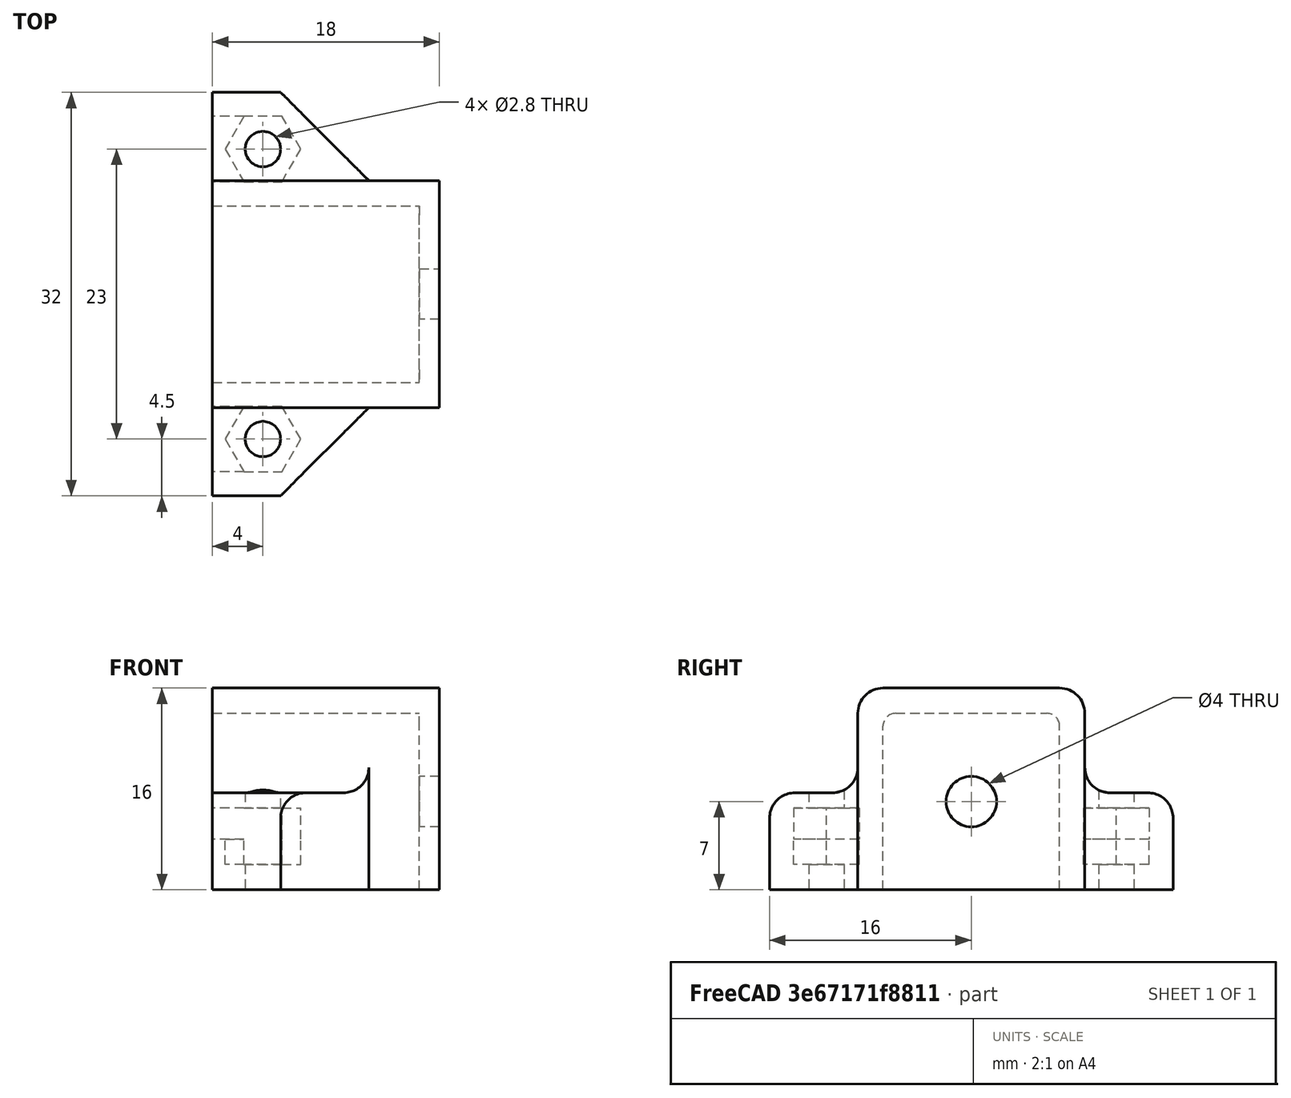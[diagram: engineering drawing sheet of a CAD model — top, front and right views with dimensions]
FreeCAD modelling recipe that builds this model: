
FCSTD DOCUMENT  (FreeCAD 0.19R24276 (Git))
Label: PB3D_TriPlate_MotWireRet
License: All rights reserved
LicenseURL: http://en.wikipedia.org/wiki/All_rights_reserved
objects: Sketcher::SketchObject×8, PartDesign::Pocket×6, PartDesign::Plane×2, Spreadsheet::Sheet×1, PartDesign::Pad×1, PartDesign::Body×1, App::Part×1, Mesh::Feature×1
note: 25 computed .brp shape members not serialized (recipe doc carries the construction recipe); baked Part::Feature solids carry a one-line shape summary decoded from their .brp

FEATURE [Spreadsheet::Sheet] Spreadsheet  label="params"
  cells = A2=M2 Bolt Clearances; C2=M2.5 Bolt Clearances; E2=M3 Bolt Clearances; A3=Hole Clear Diam; B3(m2_hole_clear_diam)==2.5mm; C3=Hole Clear Diam; D3(m25_hole_clear_diam)==2.8mm; E3=Hole Clear Diam; F3(m3_hole_clear_diam)==3.3mm; A4=Head Clear Diam; B4(m2_head_clear_diam)==4mm; C4=Head Clear Diam; D4(m25_head_clear_diam)==5mm; E4=Head Clear Diam; F4(m3_head_clear_diam)==6.1mm; A5=Head Min Depth; B5(m2_head_min_depth)==1.3mm; C5=Head Min Depth; D5(m25_head_min_depth)==1.6mm; E5=Head Min Depth; F5(m3_head_min_depth)==1.8mm; A6=Nut Clear Flat; B6(m2_nut_clear_flat)==4.2mm; C6=Nut Clear Flat; D6(m25_nut_clear_flat)==5.2mm; E6=Nut Clear Flat; F6(m3_nut_clear_flat)==5.8mm; A7=Nut Min Depth; B7(m2_nut_min_depth)==1.75mm; C7=Nut Min Depth; D7(m25_nut_min_depth)==2mm; E7=Nut Min Depth; F7(m3_nut_min_depth)==2.4mm; A9=Mot Wire Ret Dims; A10=Std Rad; B10(std_rad)==2mm; C10=Foot Width; D10(foot_width)==7mm; E10=Hole Loc L; F10(hole_loc_l)==4mm; A11=Arch Height; B11(arch_height)==14mm; C11=Foot Height; D11(foot_height)==hsunk_z + hsunk_height + hslot_height + 1.2mm; E11=Hole Loc W; F11(hole_loc_w)==arch_width + foot_tot_width; A12=Arch Width; B12(arch_width)==14mm; E12=Hex Sunk Z; F12(hsunk_z)==2mm; A13=Arch Leng; B13(arch_leng)==18mm; C13=Foot Tot Width; D13(foot_tot_width)==foot_width + arch_wallthick; E13=Hex Sunk Height; F13(hsunk_height)==m25_nut_min_depth; A14=Arch Wall Thick; B14(arch_wallthick)==2mm; E14=Hex Slot Z; F14(hslot_z)==hsunk_z + hsunk_height; C15=Back Wall Thick; D15(back_wall_thick)==1.6mm; E15=Hex Slot Height; F15(hslot_height)==m25_nut_min_depth + 0.5mm; A16=Tot Width; B16(tot_width)==arch_width + 2 * foot_width + 2 * arch_wallthick
FEATURE [Sketcher::SketchObject] Sketch
  FullyConstrained = true
  MapMode = 5
  Placement = pos=(0,0,0) rot=(0.57735,0.57735,0.57735;2.0944rad)
  Support = -> [YZ_Plane001]
  expr: Constraints[42] = <<params>>.std_rad
  expr: Constraints[46] = <<params>>.arch_wallthick
  expr: Constraints[43] = <<params>>.arch_width
  expr: Constraints[50] = <<params>>.foot_width
  expr: Constraints[44] = <<params>>.arch_height
  expr: Constraints[48] = <<params>>.std_rad / 2
  expr: Constraints[45] = <<params>>.arch_wallthick
  expr: Constraints[51] = <<params>>.foot_height
  sketch-geometry (22):
    g0: LineSegment StartX=-16 StartY=0 StartZ=0 EndX=-7 EndY=0 EndZ=0
    g1: LineSegment StartX=7 StartY=0 StartZ=0 EndX=16 EndY=0 EndZ=0
    g2: LineSegment StartX=-7 StartY=0 StartZ=0 EndX=-7 EndY=13 EndZ=0
    g3: LineSegment StartX=-6 StartY=14 StartZ=0 EndX=6 EndY=14 EndZ=0
    g4: LineSegment StartX=7 StartY=0 StartZ=0 EndX=7 EndY=13 EndZ=0
    g5: LineSegment StartX=-16 StartY=0 StartZ=0 EndX=-16 EndY=5.7 EndZ=0
    g6: LineSegment StartX=-14 StartY=7.7 StartZ=0 EndX=-11 EndY=7.7 EndZ=0
    g7: LineSegment StartX=-9 StartY=9.7 StartZ=0 EndX=-9 EndY=14 EndZ=0
    g8: LineSegment StartX=-7 StartY=16 StartZ=0 EndX=7 EndY=16 EndZ=0
    g9: LineSegment StartX=9 StartY=14 StartZ=0 EndX=9 EndY=9.7 EndZ=0
    g10: LineSegment StartX=11 StartY=7.7 StartZ=0 EndX=14 EndY=7.7 EndZ=0
    g11: LineSegment StartX=16 StartY=5.7 StartZ=0 EndX=16 EndY=0 EndZ=0
    g12: LineSegment StartX=0 StartY=0 StartZ=0 EndX=0 EndY=16 EndZ=0
    g13: ArcOfCircle CenterX=-6 CenterY=13 CenterZ=0 NormalX=0 NormalY=0 NormalZ=1 AngleXU=0 Radius=1 StartAngle=1.5708 EndAngle=3.14159
    g14: ArcOfCircle CenterX=6 CenterY=13 CenterZ=0 NormalX=0 NormalY=0 NormalZ=1 AngleXU=0 Radius=1 StartAngle=-9e-16 EndAngle=1.5708
    g15: ArcOfCircle CenterX=7 CenterY=14 CenterZ=0 NormalX=0 NormalY=0 NormalZ=1 AngleXU=0 Radius=2 StartAngle=0 EndAngle=1.5708
    g16: ArcOfCircle CenterX=-7 CenterY=14 CenterZ=0 NormalX=0 NormalY=0 NormalZ=1 AngleXU=0 Radius=2 StartAngle=1.5708 EndAngle=3.14159
    g17: ArcOfCircle CenterX=11 CenterY=9.7 CenterZ=0 NormalX=0 NormalY=0 NormalZ=1 AngleXU=0 Radius=2 StartAngle=3.14159 EndAngle=4.71239
    g18: ArcOfCircle CenterX=14 CenterY=5.7 CenterZ=0 NormalX=0 NormalY=0 NormalZ=1 AngleXU=0 Radius=2 StartAngle=1e-16 EndAngle=1.5708
    g19: ArcOfCircle CenterX=-14 CenterY=5.7 CenterZ=0 NormalX=0 NormalY=0 NormalZ=1 AngleXU=0 Radius=2 StartAngle=1.5708 EndAngle=3.14159
    g20: ArcOfCircle CenterX=-11 CenterY=9.7 CenterZ=0 NormalX=0 NormalY=0 NormalZ=1 AngleXU=0 Radius=2 StartAngle=4.71239 EndAngle=6.28319
    g21: LineSegment StartX=-7 StartY=0 StartZ=0 EndX=7 EndY=0 EndZ=0
  constraints (55):
    c: PointOnObject(g0,g-1)
    c: PointOnObject(g0,g-1)
    c: PointOnObject(g1,g-1)
    c: Equal(g1,g0)
    c: Symmetric(g0,g1,g-1)
    c: Coincident(g2,g0)
    c: Vertical(g2)
    c: Horizontal(g3)
    c: Coincident(g4,g1)
    c: Vertical(g4)
    c: Coincident(g5,g0)
    c: Vertical(g5)
    c: Horizontal(g6)
    c: Vertical(g7)
    c: Horizontal(g8)
    c: Vertical(g9)
    c: Horizontal(g10)
    c: Coincident(g11,g1)
    c: Vertical(g11)
    c: Coincident(g12,g-1)
    c: PointOnObject(g12,g-2)
    c: Tangent(g2,g13) = 1.5708
    c: Tangent(g3,g13) = 1.5708
    c: Tangent(g3,g14) = 1.5708
    c: Tangent(g4,g14) = -1.5708
    c: Tangent(g9,g15) = 1.5708
    c: Tangent(g8,g15) = 1.5708
    c: Tangent(g8,g16) = 1.5708
    c: Tangent(g7,g16) = 1.5708
    c: Tangent(g9,g17) = -1.5708
    c: Tangent(g10,g17) = -1.5708
    c: Tangent(g10,g18) = 1.5708
    c: Tangent(g11,g18) = 1.5708
    c: Tangent(g6,g19) = 1.5708
    c: Tangent(g5,g19) = 1.5708
    c: Tangent(g7,g20) = -1.5708
    c: Tangent(g6,g20) = -1.5708
    c: Symmetric(g8,g8,g12)
    c: Equal(g18,g17)
    c: Equal(g17,g15)
    c: Equal(g16,g20)
    c: Equal(g20,g19)
    c: Radius(g18) = 2
    c: DistanceX(g0,g1) = 14
    c: DistanceY(g-1,g3) = 14
    c: DistanceY(g3,g8) = 2
    c: DistanceX(g4,g9) = 2
    c: Equal(g13,g14)
    c: Radius(g14) = 1
    c: Equal(g16,g15)
    c: DistanceX(g9,g1) = 7
    c: DistanceY(g1,g10) = 7.7
    c: Equal(g11,g5)
    c: Coincident(g21,g1)
    c: Coincident(g21,g0)
FEATURE [PartDesign::Pad] Pad  label="MainExt"
  Direction = (1,1,1)
  Length = 18
  Length2 = 100
  Placement = pos=(0,0,0) rot=(0.57735,0.57735,0.57735;2.0944rad)
  Profile = -> Sketch
  Type = 0
  expr: Length = <<params>>.arch_leng
FEATURE [PartDesign::Plane] DatumPlane  label="Datum_HexSunk"
  AttachmentOffset = pos=(0,0,2) rot=(0,0,1;0rad)
  Length = 60
  MapMode = 5
  Placement = pos=(0,0,2) rot=(0,0,1;0rad)
  ResizeMode = 0
  Support = -> [XY_Plane001]
  Width = 60
  expr: .AttachmentOffset.Base.z = <<params>>.hsunk_z
FEATURE [PartDesign::Plane] DatumPlane001  label="Datum_HexSlot"
  AttachmentOffset = pos=(0,0,4) rot=(0,0,1;0rad)
  Length = 60
  MapMode = 5
  Placement = pos=(0,0,4) rot=(0,0,1;0rad)
  ResizeMode = 0
  Support = -> [XY_Plane001]
  Width = 60
  expr: .AttachmentOffset.Base.z = <<params>>.hslot_z
FEATURE [Sketcher::SketchObject] Sketch001  label="HoleLoc_Temp"
  FullyConstrained = true
  MapMode = 5
  Support = -> [XY_Plane001]
  expr: Constraints[5] = <<params>>.hole_loc_w
  expr: Constraints[4] = <<params>>.hole_loc_l
  sketch-geometry (2):
    g0: LineSegment StartX=0 StartY=0 StartZ=0 EndX=4 EndY=0 EndZ=0
    g1: LineSegment StartX=4 StartY=11.5 StartZ=0 EndX=4 EndY=-11.5 EndZ=0
  constraints (6):
    c: Coincident(g0,g-1)
    c: PointOnObject(g0,g-1)
    c: Vertical(g1)
    c: Symmetric(g1,g1,g0)
    c: DistanceX(g-1,g0) = 4
    c: DistanceY(g1,g1) = 23
FEATURE [Sketcher::SketchObject] Sketch002  label="HoleLoc"
  FullyConstrained = true
  MapMode = 5
  Support = -> [XY_Plane001]
  expr: Constraints[9] = <<params>>.m25_hole_clear_diam
  expr: Constraints[4] = <<params>>.hole_loc_l
  expr: Constraints[5] = <<params>>.hole_loc_w
  sketch-geometry (4):
    g0: LineSegment StartX=0 StartY=0 StartZ=0 EndX=4 EndY=0 EndZ=0
    g1: LineSegment StartX=4 StartY=11.5 StartZ=0 EndX=4 EndY=-11.5 EndZ=0
    g2: Circle CenterX=4 CenterY=11.5 CenterZ=0 NormalX=0 NormalY=0 NormalZ=1 AngleXU=0 Radius=1.4
    g3: Circle CenterX=4 CenterY=-11.5 CenterZ=0 NormalX=0 NormalY=0 NormalZ=1 AngleXU=0 Radius=1.4
  constraints (10):
    c: Coincident(g0,g-1)
    c: PointOnObject(g0,g-1)
    c: Vertical(g1)
    c: Symmetric(g1,g1,g0)
    c: DistanceX(g-1,g0) = 4
    c: DistanceY(g1,g1) = 23
    c: Coincident(g2,g1)
    c: Coincident(g3,g1)
    c: Equal(g2,g3)
    c: Diameter(g2) = 2.8
FEATURE [PartDesign::Pocket] Pocket  label="MtHoles"
  BaseFeature = -> Pad
  Length = 5
  Length2 = 100
  Placement = pos=(0,0,0) rot=(0.57735,0.57735,0.57735;2.0944rad)
  Profile = -> Sketch002
  Reversed = true
  Type = 1
FEATURE [Sketcher::SketchObject] Sketch003  label="HSunk"
  FullyConstrained = true
  MapMode = 5
  Placement = pos=(0,0,2) rot=(0,0,1;0rad)
  Support = -> [DatumPlane]
  expr: Constraints[45] = <<params>>.m25_nut_clear_flat
  expr: Constraints[4] = <<params>>.hole_loc_l
  expr: Constraints[5] = <<params>>.hole_loc_w
  sketch-geometry (16):
    g0: LineSegment StartX=0 StartY=0 StartZ=0 EndX=4 EndY=0 EndZ=0
    g1: LineSegment StartX=4 StartY=11.5 StartZ=0 EndX=4 EndY=-11.5 EndZ=0
    g2: LineSegment StartX=0.997779 StartY=11.5 StartZ=0 EndX=2.49889 EndY=8.9 EndZ=0
    g3: LineSegment StartX=2.49889 StartY=8.9 StartZ=0 EndX=5.50111 EndY=8.9 EndZ=0
    g4: LineSegment StartX=5.50111 StartY=8.9 StartZ=0 EndX=7.00222 EndY=11.5 EndZ=0
    g5: LineSegment StartX=7.00222 StartY=11.5 StartZ=0 EndX=5.50111 EndY=14.1 EndZ=0
    g6: LineSegment StartX=5.50111 StartY=14.1 StartZ=0 EndX=2.49889 EndY=14.1 EndZ=0
    g7: LineSegment StartX=2.49889 StartY=14.1 StartZ=0 EndX=0.997779 EndY=11.5 EndZ=0
    g8: Circle CenterX=4 CenterY=11.5 CenterZ=0 NormalX=0 NormalY=0 NormalZ=1 AngleXU=0 Radius=3.00222
    g9: LineSegment StartX=7.00222 StartY=-11.5 StartZ=0 EndX=5.50111 EndY=-8.9 EndZ=0
    g10: LineSegment StartX=5.50111 StartY=-8.9 StartZ=0 EndX=2.49889 EndY=-8.9 EndZ=0
    g11: LineSegment StartX=2.49889 StartY=-8.9 StartZ=0 EndX=0.997779 EndY=-11.5 EndZ=0
    g12: LineSegment StartX=0.997779 StartY=-11.5 StartZ=0 EndX=2.49889 EndY=-14.1 EndZ=0
    g13: LineSegment StartX=2.49889 StartY=-14.1 StartZ=0 EndX=5.50111 EndY=-14.1 EndZ=0
    g14: LineSegment StartX=5.50111 StartY=-14.1 StartZ=0 EndX=7.00222 EndY=-11.5 EndZ=0
    g15: Circle CenterX=4 CenterY=-11.5 CenterZ=0 NormalX=0 NormalY=0 NormalZ=1 AngleXU=0 Radius=3.00222
  constraints (38):
    c: Coincident(g0,g-1)
    c: PointOnObject(g0,g-1)
    c: Vertical(g1)
    c: Symmetric(g1,g1,g0)
    c: DistanceX(g-1,g0) = 4
    c: DistanceY(g1,g1) = 23
    c: Coincident(g2,g3)
    c: Coincident(g3,g4)
    c: Coincident(g4,g5)
    c: Coincident(g5,g6)
    c: Coincident(g6,g7)
    c: Coincident(g7,g2)
    c: Equal(g2, g3-g7) x5
    c: PointOnObject(g2,g8)
    c: PointOnObject(g3,g8)
    c: PointOnObject(g4,g8)
    c: PointOnObject(g5,g8)
    c: PointOnObject(g6,g8)
    c: PointOnObject(g7,g8)
    c: Coincident(g8,g1)
    c: Coincident(g9,g10)
    c: Coincident(g10,g11)
    c: Coincident(g11,g12)
    c: Coincident(g12,g13)
    c: Coincident(g13,g14)
    c: Coincident(g14,g9)
    c: Equal(g9, g10-g14) x5
    c: PointOnObject(g9,g15)
    c: PointOnObject(g10,g15)
    c: PointOnObject(g11,g15)
    c: PointOnObject(g12,g15)
    c: PointOnObject(g13,g15)
    c: PointOnObject(g14,g15)
    c: Coincident(g15,g1)
    c: Horizontal(g6)
    c: Horizontal(g10)
    c: Equal(g8,g15)
    c: DistanceY(g2,g6) = 5.2
FEATURE [PartDesign::Pocket] Pocket001  label="HexSunk"
  BaseFeature = -> Pocket
  Length = 2
  Length2 = 100
  Placement = pos=(0,0,0) rot=(0.57735,0.57735,0.57735;2.0944rad)
  Profile = -> Sketch003
  Reversed = true
  Type = 0
  expr: Length = <<params>>.hsunk_height
FEATURE [Sketcher::SketchObject] Sketch004  label="Sketch_HSlot"
  FullyConstrained = true
  MapMode = 5
  Placement = pos=(0,0,4) rot=(0,0,1;0rad)
  Support = -> [DatumPlane001]
  expr: Constraints[53] = <<params>>.m25_nut_clear_flat
  expr: Constraints[4] = <<params>>.hole_loc_l
  expr: Constraints[5] = <<params>>.hole_loc_w
  sketch-geometry (19):
    g0: LineSegment StartX=0 StartY=0 StartZ=0 EndX=4 EndY=0 EndZ=0
    g1: LineSegment StartX=4 StartY=11.5 StartZ=0 EndX=4 EndY=-11.5 EndZ=0
    g2: LineSegment StartX=7.00222 StartY=11.5 StartZ=0 EndX=5.50111 EndY=14.1 EndZ=0
    g3: LineSegment StartX=5.50111 StartY=14.1 StartZ=0 EndX=2.49889 EndY=14.1 EndZ=0
    g4: LineSegment StartX=2.49889 StartY=8.9 StartZ=0 EndX=5.50111 EndY=8.9 EndZ=0
    g5: LineSegment StartX=5.50111 StartY=8.9 StartZ=0 EndX=7.00222 EndY=11.5 EndZ=0
    g6: Circle CenterX=4 CenterY=11.5 CenterZ=0 NormalX=0 NormalY=0 NormalZ=1 AngleXU=0 Radius=3.00222
    g7: LineSegment StartX=7.00222 StartY=-11.5 StartZ=0 EndX=5.50111 EndY=-8.9 EndZ=0
    g8: LineSegment StartX=5.50111 StartY=-8.9 StartZ=0 EndX=2.49889 EndY=-8.9 EndZ=0
    g9: LineSegment StartX=2.49889 StartY=-14.1 StartZ=0 EndX=5.50111 EndY=-14.1 EndZ=0
    g10: LineSegment StartX=5.50111 StartY=-14.1 StartZ=0 EndX=7.00222 EndY=-11.5 EndZ=0
    g11: Circle CenterX=4 CenterY=-11.5 CenterZ=0 NormalX=0 NormalY=0 NormalZ=1 AngleXU=0 Radius=3.00222
    g12: LineSegment StartX=2.49889 StartY=14.1 StartZ=0 EndX=-7.50111 EndY=14.1 EndZ=0
    g13: LineSegment StartX=2.49889 StartY=8.9 StartZ=0 EndX=-7.50111 EndY=8.9 EndZ=0
    g14: LineSegment StartX=-7.50111 StartY=8.9 StartZ=0 EndX=-7.50111 EndY=14.1 EndZ=0
    g15: LineSegment StartX=2.49889 StartY=-14.1 StartZ=0 EndX=-7.50111 EndY=-14.1 EndZ=0
    g16: LineSegment StartX=2.49889 StartY=-8.9 StartZ=0 EndX=-7.50111 EndY=-8.9 EndZ=0
    g17: LineSegment StartX=-7.50111 StartY=-14.1 StartZ=0 EndX=-7.50111 EndY=-8.9 EndZ=0
    g18: LineSegment StartX=-7.50111 StartY=-8.9 StartZ=0 EndX=-7.50111 EndY=8.9 EndZ=0
  constraints (54):
    c: Coincident(g0,g-1)
    c: PointOnObject(g0,g-1)
    c: Vertical(g1)
    c: Symmetric(g1,g1,g0)
    c: DistanceX(g-1,g0) = 4
    c: DistanceY(g1,g1) = 23
    c: Coincident(g2,g3)
    c: Coincident(g4,g5)
    c: Coincident(g5,g2)
    c: Equal(g2,g3)
    c: Equal(g2,g4)
    c: Equal(g2,g5)
    c: PointOnObject(g2,g6)
    c: PointOnObject(g3,g6)
    c: PointOnObject(g4,g6)
    c: PointOnObject(g4,g6)
    c: PointOnObject(g5,g6)
    c: Coincident(g6,g1)
    c: Coincident(g7,g8)
    c: Coincident(g9,g10)
    c: Coincident(g10,g7)
    c: Equal(g7,g8)
    c: Equal(g7,g9)
    c: Equal(g7,g10)
    c: PointOnObject(g7,g11)
    c: PointOnObject(g8,g11)
    c: PointOnObject(g9,g11)
    c: PointOnObject(g9,g11)
    c: PointOnObject(g10,g11)
    c: Coincident(g11,g1)
    c: Horizontal(g3)
    c: Horizontal(g8)
    c: Equal(g6,g11)
    c: Horizontal(g9)
    c: Horizontal(g4)
    c: Coincident(g12,g3)
    c: Horizontal(g12)
    c: Coincident(g13,g4)
    c: Horizontal(g13)
    c: Coincident(g14,g13)
    c: Coincident(g14,g12)
    c: Vertical(g14)
    c: Coincident(g15,g9)
    c: Horizontal(g15)
    c: Coincident(g16,g8)
    c: Horizontal(g16)
    c: Coincident(g17,g15)
    c: Coincident(g17,g16)
    c: Vertical(g17)
    c: Coincident(g18,g16)
    c: Coincident(g18,g13)
    c: Vertical(g18)
    c: Distance(g15) = 10
    c: DistanceY(g9,g7) = 5.2
FEATURE [PartDesign::Pocket] Pocket002  label="HexSlot"
  BaseFeature = -> Pocket001
  Length = 2.5
  Length2 = 100
  Placement = pos=(0,0,0) rot=(0.57735,0.57735,0.57735;2.0944rad)
  Profile = -> Sketch004
  Reversed = true
  Type = 0
  expr: Length = <<params>>.hslot_height
FEATURE [Sketcher::SketchObject] Sketch005
  FullyConstrained = true
  MapMode = 5
  Support = -> [XY_Plane001]
  expr: Constraints[31] = <<params>>.hole_loc_l + <<params>>.m25_hole_clear_diam / 2
  expr: Constraints[30] = <<params>>.arch_leng
  expr: Constraints[29] = <<params>>.foot_width
  expr: Constraints[27] = <<params>>.arch_width + <<params>>.arch_wallthick * 2
  sketch-geometry (12):
    g0: LineSegment StartX=12.4 StartY=9 StartZ=0 EndX=5.4 EndY=16 EndZ=0
    g1: LineSegment StartX=5.4 StartY=16 StartZ=0 EndX=23.4 EndY=16 EndZ=0
    g2: LineSegment StartX=12.4 StartY=9 StartZ=0 EndX=23.4 EndY=9 EndZ=0
    g3: LineSegment StartX=23.4 StartY=16 StartZ=0 EndX=23.4 EndY=9 EndZ=0
    g4: LineSegment StartX=0 StartY=0 StartZ=0 EndX=12.4 EndY=0 EndZ=0
    g5: LineSegment StartX=12.4 StartY=9 StartZ=0 EndX=12.4 EndY=-9 EndZ=0
    g6: LineSegment StartX=12.4 StartY=-9 StartZ=0 EndX=23.4 EndY=-9 EndZ=0
    g7: LineSegment StartX=23.4 StartY=-9 StartZ=0 EndX=23.4 EndY=-16 EndZ=0
    g8: LineSegment StartX=12.4 StartY=-9 StartZ=0 EndX=5.4 EndY=-16 EndZ=0
    g9: LineSegment StartX=5.4 StartY=-16 StartZ=0 EndX=23.4 EndY=-16 EndZ=0
    g10: LineSegment StartX=23.4 StartY=9 StartZ=0 EndX=23.4 EndY=-9 EndZ=0
    g11: LineSegment StartX=5.4 StartY=16 StartZ=0 EndX=5.4 EndY=-16 EndZ=0
  constraints (32):
    c: Coincident(g1,g0)
    c: Horizontal(g1)
    c: Coincident(g2,g0)
    c: Horizontal(g2)
    c: Coincident(g3,g1)
    c: Coincident(g3,g2)
    c: Vertical(g3)
    c: Coincident(g4,g-1)
    c: PointOnObject(g4,g-1)
    c: Coincident(g5,g0)
    c: Vertical(g5)
    c: Symmetric(g0,g5,g4)
    c: Coincident(g6,g5)
    c: Horizontal(g6)
    c: Coincident(g7,g6)
    c: Vertical(g7)
    c: Coincident(g8,g6)
    c: Coincident(g9,g8)
    c: Coincident(g9,g7)
    c: Horizontal(g9)
    c: Coincident(g10,g2)
    c: Coincident(g10,g6)
    c: Vertical(g10)
    c: Coincident(g11,g0)
    c: Coincident(g11,g8)
    c: Vertical(g11)
    c: Equal(g0,g8)
    c: DistanceY(g6,g2) = 18
    c: Angle(g8,g11) = 0.785398
    c: DistanceY(g7,g6) = 7
    c: DistanceX(g8,g7) = 18
    c: DistanceX(g-1,g8) = 5.4
FEATURE [PartDesign::Pocket] Pocket003  label="SculptZ"
  BaseFeature = -> Pocket002
  Length = 5
  Length2 = 100
  Placement = pos=(0,0,0) rot=(0.57735,0.57735,0.57735;2.0944rad)
  Profile = -> Sketch005
  Reversed = true
  Type = 1
FEATURE [Sketcher::SketchObject] Sketch006
  FullyConstrained = true
  MapMode = 5
  Placement = pos=(0,0,0) rot=(0.57735,0.57735,0.57735;2.0944rad)
  Support = -> [YZ_Plane001]
  expr: Constraints[51] = <<params>>.foot_height
  expr: Constraints[45] = <<params>>.arch_wallthick
  expr: Constraints[48] = <<params>>.std_rad / 2
  expr: Constraints[44] = <<params>>.arch_height
  expr: Constraints[50] = <<params>>.foot_width
  expr: Constraints[43] = <<params>>.arch_width
  expr: Constraints[46] = <<params>>.arch_wallthick
  expr: Constraints[42] = <<params>>.std_rad
  sketch-geometry (22):
    g0: LineSegment StartX=-16 StartY=0 StartZ=0 EndX=-7 EndY=0 EndZ=0
    g1: LineSegment StartX=7 StartY=0 StartZ=0 EndX=16 EndY=0 EndZ=0
    g2: LineSegment StartX=-7 StartY=0 StartZ=0 EndX=-7 EndY=13 EndZ=0
    g3: LineSegment StartX=-6 StartY=14 StartZ=0 EndX=6 EndY=14 EndZ=0
    g4: LineSegment StartX=7 StartY=0 StartZ=0 EndX=7 EndY=13 EndZ=0
    g5: LineSegment StartX=-16 StartY=0 StartZ=0 EndX=-16 EndY=5.7 EndZ=0
    g6: LineSegment StartX=-14 StartY=7.7 StartZ=0 EndX=-11 EndY=7.7 EndZ=0
    g7: LineSegment StartX=-9 StartY=9.7 StartZ=0 EndX=-9 EndY=14 EndZ=0
    g8: LineSegment StartX=-7 StartY=16 StartZ=0 EndX=7 EndY=16 EndZ=0
    g9: LineSegment StartX=9 StartY=14 StartZ=0 EndX=9 EndY=9.7 EndZ=0
    g10: LineSegment StartX=11 StartY=7.7 StartZ=0 EndX=14 EndY=7.7 EndZ=0
    g11: LineSegment StartX=16 StartY=5.7 StartZ=0 EndX=16 EndY=0 EndZ=0
    g12: LineSegment StartX=0 StartY=0 StartZ=0 EndX=0 EndY=16 EndZ=0
    g13: ArcOfCircle CenterX=-6 CenterY=13 CenterZ=0 NormalX=0 NormalY=0 NormalZ=1 AngleXU=0 Radius=1 StartAngle=1.5708 EndAngle=3.14159
    g14: ArcOfCircle CenterX=6 CenterY=13 CenterZ=0 NormalX=0 NormalY=0 NormalZ=1 AngleXU=0 Radius=1 StartAngle=-9e-16 EndAngle=1.5708
    g15: ArcOfCircle CenterX=7 CenterY=14 CenterZ=0 NormalX=0 NormalY=0 NormalZ=1 AngleXU=0 Radius=2 StartAngle=0 EndAngle=1.5708
    g16: ArcOfCircle CenterX=-7 CenterY=14 CenterZ=0 NormalX=0 NormalY=0 NormalZ=1 AngleXU=0 Radius=2 StartAngle=1.5708 EndAngle=3.14159
    g17: ArcOfCircle CenterX=11 CenterY=9.7 CenterZ=0 NormalX=0 NormalY=0 NormalZ=1 AngleXU=0 Radius=2 StartAngle=3.14159 EndAngle=4.71239
    g18: ArcOfCircle CenterX=14 CenterY=5.7 CenterZ=0 NormalX=0 NormalY=0 NormalZ=1 AngleXU=0 Radius=2 StartAngle=1e-16 EndAngle=1.5708
    g19: ArcOfCircle CenterX=-14 CenterY=5.7 CenterZ=0 NormalX=0 NormalY=0 NormalZ=1 AngleXU=0 Radius=2 StartAngle=1.5708 EndAngle=3.14159
    g20: ArcOfCircle CenterX=-11 CenterY=9.7 CenterZ=0 NormalX=0 NormalY=0 NormalZ=1 AngleXU=0 Radius=2 StartAngle=4.71239 EndAngle=6.28319
    g21: LineSegment StartX=-7 StartY=0 StartZ=0 EndX=7 EndY=0 EndZ=0
  constraints (55):
    c: PointOnObject(g0,g-1)
    c: PointOnObject(g0,g-1)
    c: PointOnObject(g1,g-1)
    c: Equal(g1,g0)
    c: Symmetric(g0,g1,g-1)
    c: Coincident(g2,g0)
    c: Vertical(g2)
    c: Horizontal(g3)
    c: Coincident(g4,g1)
    c: Vertical(g4)
    c: Coincident(g5,g0)
    c: Vertical(g5)
    c: Horizontal(g6)
    c: Vertical(g7)
    c: Horizontal(g8)
    c: Vertical(g9)
    c: Horizontal(g10)
    c: Coincident(g11,g1)
    c: Vertical(g11)
    c: Coincident(g12,g-1)
    c: PointOnObject(g12,g-2)
    c: Tangent(g2,g13) = 1.5708
    c: Tangent(g3,g13) = 1.5708
    c: Tangent(g3,g14) = 1.5708
    c: Tangent(g4,g14) = -1.5708
    c: Tangent(g9,g15) = 1.5708
    c: Tangent(g8,g15) = 1.5708
    c: Tangent(g8,g16) = 1.5708
    c: Tangent(g7,g16) = 1.5708
    c: Tangent(g9,g17) = -1.5708
    c: Tangent(g10,g17) = -1.5708
    c: Tangent(g10,g18) = 1.5708
    c: Tangent(g11,g18) = 1.5708
    c: Tangent(g6,g19) = 1.5708
    c: Tangent(g5,g19) = 1.5708
    c: Tangent(g7,g20) = -1.5708
    c: Tangent(g6,g20) = -1.5708
    c: Symmetric(g8,g8,g12)
    c: Equal(g18,g17)
    c: Equal(g17,g15)
    c: Equal(g16,g20)
    c: Equal(g20,g19)
    c: Radius(g18) = 2
    c: DistanceX(g0,g1) = 14
    c: DistanceY(g-1,g3) = 14
    c: DistanceY(g3,g8) = 2
    c: DistanceX(g4,g9) = 2
    c: Equal(g13,g14)
    c: Radius(g14) = 1
    c: Equal(g16,g15)
    c: DistanceX(g9,g1) = 7
    c: DistanceY(g1,g10) = 7.7
    c: Equal(g11,g5)
    c: Coincident(g21,g1)
    c: Coincident(g21,g0)
FEATURE [PartDesign::Pocket] Pocket004  label="ArchCut"
  BaseFeature = -> Pocket003
  Length = 16.4
  Length2 = 100
  Placement = pos=(0,0,0) rot=(0.57735,0.57735,0.57735;2.0944rad)
  Profile = -> Sketch006
  Reversed = true
  Type = 0
  expr: Length = <<params>>.arch_leng - <<params>>.back_wall_thick
FEATURE [Sketcher::SketchObject] Sketch007
  FullyConstrained = true
  MapMode = 5
  Placement = pos=(0,0,0) rot=(0.57735,0.57735,0.57735;2.0944rad)
  Support = -> [YZ_Plane001]
  expr: Constraints[2] = <<params>>.arch_height / 2
  sketch-geometry (1):
    g0: Circle CenterX=0 CenterY=7 CenterZ=0 NormalX=0 NormalY=0 NormalZ=1 AngleXU=0 Radius=2
  constraints (3):
    c: PointOnObject(g0,g-2)
    c: Diameter(g0) = 4
    c: DistanceY(g-1,g0) = 7
FEATURE [PartDesign::Pocket] Pocket005  label="BackWallHole"
  BaseFeature = -> Pocket004
  Length = 5
  Length2 = 100
  Placement = pos=(0,0,0) rot=(0.57735,0.57735,0.57735;2.0944rad)
  Profile = -> Sketch007
  Reversed = true
  Type = 1
FEATURE [PartDesign::Body] Body  label="PB3D_MotWireRet"
  Group = -> [Sketch,Pad,DatumPlane,DatumPlane001,Sketch001,Sketch002,Pocket,Sketch003,Pocket001,Sketch004,Pocket002,Sketch005,Pocket003,Sketch006,Pocket004,Sketch007,Pocket005]
  Origin = -> Origin001
  Tip = -> Pocket005
FEATURE [App::Part] Part  label="PB3D_MotWireRetPart"
  Group = -> [Body]
  Origin = -> Origin
FEATURE [Mesh::Feature] Mesh  label="PB3D_MotWireRet (Meshed)"
